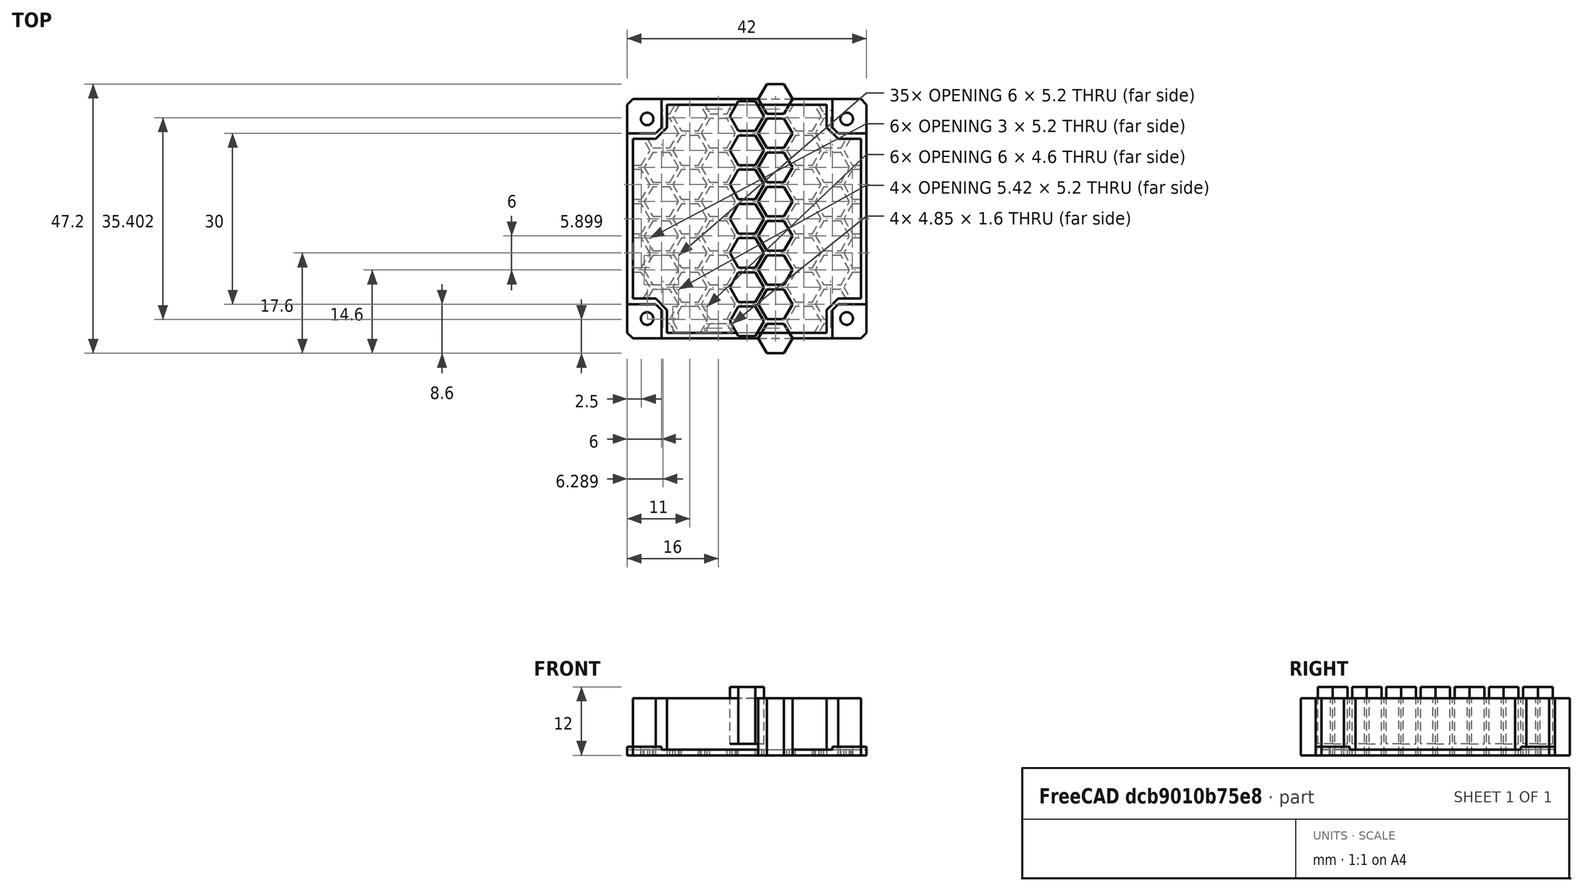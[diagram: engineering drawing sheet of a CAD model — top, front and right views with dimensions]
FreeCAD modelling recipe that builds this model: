
FCSTD DOCUMENT  (FreeCAD 0.18R14555 (Git shallow))
Label: 4010-blower-fin
License: All rights reserved
LicenseURL: http://en.wikipedia.org/wiki/All_rights_reserved
objects: Part::Feature×26, Part::Box×5, Part::Chamfer×5, Part::MultiFuse×5, Part::Cylinder×4, Part::Cut×2, Sketcher::SketchObject×1, PartDesign::Pad×1, PartDesign::Body×1, Part::MultiCommon×1
note: 52 computed .brp shape members not serialized (recipe doc carries the construction recipe); baked Part::Feature solids carry a one-line shape summary decoded from their .brp

FEATURE [Part::Box] Box  label="Cube"
  AttacherType = Attacher::AttachEngine3D
  Height = 1
  Length = 42
  Placement = pos=(-21,-21,0) rot=(0,0,1;0rad)
  Width = 42
FEATURE [Part::Box] Box001  label="Cube001"
  AttacherType = Attacher::AttachEngine3D
  Height = 1.5
  Length = 6
  Placement = pos=(-21,-21,0) rot=(0,0,1;0rad)
  Width = 6
FEATURE [Part::Box] Box002  label="Cube002"
  AttacherType = Attacher::AttachEngine3D
  Height = 1.5
  Length = 6
  Placement = pos=(-21,15,0) rot=(0,0,1;0rad)
  Width = 6
FEATURE [Part::Box] Box003  label="Cube003"
  AttacherType = Attacher::AttachEngine3D
  Height = 1.5
  Length = 6
  Placement = pos=(15,15,0) rot=(0,0,1;0rad)
  Width = 6
FEATURE [Part::Box] Box004  label="Cube004"
  AttacherType = Attacher::AttachEngine3D
  Height = 1.5
  Length = 6
  Placement = pos=(15,-21,0) rot=(0,0,1;0rad)
  Width = 6
FEATURE [Part::Cylinder] Cylinder
  Angle = 360
  AttacherType = Attacher::AttachEngine3D
  Height = 10
  Placement = pos=(-17.5,17.5,0) rot=(0,0,1;0rad)
  Radius = 1.1
FEATURE [Part::Cylinder] Cylinder001
  Angle = 360
  AttacherType = Attacher::AttachEngine3D
  Height = 10
  Placement = pos=(17.5,17.5,0) rot=(0,0,1;0rad)
  Radius = 1.1
FEATURE [Part::Cylinder] Cylinder002
  Angle = 360
  AttacherType = Attacher::AttachEngine3D
  Height = 10
  Placement = pos=(17.5,-17.5,0) rot=(0,0,1;0rad)
  Radius = 1.1
FEATURE [Part::Cylinder] Cylinder003
  Angle = 360
  AttacherType = Attacher::AttachEngine3D
  Height = 10
  Placement = pos=(-17.5,-17.5,0) rot=(0,0,1;0rad)
  Radius = 1.1
FEATURE [Part::Chamfer] Chamfer
  Base = -> Box002
  Edges = 1 edges r=1: [Edge5]
FEATURE [Part::Chamfer] Chamfer001
  Base = -> Box001
  Edges = 1 edges r=1: [Edge7]
FEATURE [Part::Chamfer] Chamfer002
  Base = -> Box003
  Edges = 1 edges r=1: [Edge1]
FEATURE [Part::Chamfer] Chamfer003
  Base = -> Box004
  Edges = 1 edges r=1: [Edge3]
FEATURE [Part::MultiFuse] Fusion
  Shapes = -> [Chamfer003,Chamfer,Chamfer001,Chamfer002,Box]
FEATURE [Part::Chamfer] Chamfer004
  Base = -> Fusion
  Edges = 4 edges r=1: [Edge19,Edge58,Edge60,Edge63]
FEATURE [Part::MultiFuse] Fusion001
  Shapes = -> [Cylinder003,Cylinder,Cylinder002,Cylinder001]
FEATURE [Part::Cut] Cut
  Base = -> Chamfer004
  Tool = -> Fusion001
FEATURE [Part::Feature] Body001  label="hex"
  shape: bbox 6 x 5.196 x 10 mm, 8 faces (baked)
FEATURE [Part::Feature] Body002  label="hex001"
  Placement = pos=(0,6,0) rot=(0,0,1;0rad)
  shape: bbox 6 x 5.196 x 10 mm, 8 faces (baked)
FEATURE [Part::Feature] Body003  label="hex002"
  Placement = pos=(0,12,0) rot=(0,0,1;0rad)
  shape: bbox 6 x 5.196 x 10 mm, 8 faces (baked)
FEATURE [Part::Feature] Body004  label="hex003"
  Placement = pos=(0,18,0) rot=(0,0,1;0rad)
  shape: bbox 6 x 5.196 x 10 mm, 8 faces (baked)
FEATURE [Part::Feature] Body005  label="hex004"
  Placement = pos=(0,-6,0) rot=(0,0,1;0rad)
  shape: bbox 6 x 5.196 x 10 mm, 8 faces (baked)
FEATURE [Part::Feature] Body006  label="hex005"
  Placement = pos=(0,-12,0) rot=(0,0,1;0rad)
  shape: bbox 6 x 5.196 x 10 mm, 8 faces (baked)
FEATURE [Part::Feature] Body007  label="hex006"
  Placement = pos=(0,-18,0) rot=(0,0,1;0rad)
  shape: bbox 6 x 5.196 x 10 mm, 8 faces (baked)
FEATURE [Part::Feature] Body008  label="hex007"
  Placement = pos=(5,3,0) rot=(0,0,1;0rad)
  shape: bbox 6 x 5.196 x 10 mm, 8 faces (baked)
FEATURE [Part::Feature] Body009  label="hex008"
  Placement = pos=(5,9,0) rot=(0,0,1;0rad)
  shape: bbox 6 x 5.196 x 10 mm, 8 faces (baked)
FEATURE [Part::Feature] Body010  label="hex009"
  Placement = pos=(5,15,0) rot=(0,0,1;0rad)
  shape: bbox 6 x 5.196 x 10 mm, 8 faces (baked)
FEATURE [Part::Feature] Body011  label="hex010"
  Placement = pos=(5,21,0) rot=(0,0,1;0rad)
  shape: bbox 6 x 5.196 x 10 mm, 8 faces (baked)
FEATURE [Part::Feature] Body012  label="hex011"
  Placement = pos=(5,-3,0) rot=(0,0,1;0rad)
  shape: bbox 6 x 5.196 x 10 mm, 8 faces (baked)
FEATURE [Part::Feature] Body013  label="hex012"
  Placement = pos=(5,-9,0) rot=(0,0,1;0rad)
  shape: bbox 6 x 5.196 x 10 mm, 8 faces (baked)
FEATURE [Part::Feature] Body014  label="hex013"
  Placement = pos=(5,-15,0) rot=(0,0,1;0rad)
  shape: bbox 6 x 5.196 x 10 mm, 8 faces (baked)
FEATURE [Part::Feature] Body015  label="hex014"
  Placement = pos=(5,-21,0) rot=(0,0,1;0rad)
  shape: bbox 6 x 5.196 x 10 mm, 8 faces (baked)
FEATURE [Part::MultiFuse] Fusion002
  Shapes = -> [Body011,Body010,Body009,Body008,Body012,Body013,Body014,Body015]
FEATURE [Part::MultiFuse] Fusion003
  Placement = pos=(0,0,2) rot=(0,0,1;0rad)
  Shapes = -> [Body004,Body003,Body002,Body001,Body005,Body006,Body007]
FEATURE [Part::Feature] Fusion002001  label="Fusion004"
  shape: bbox 6 x 47.2 x 10 mm, 64 faces, 8 solids (baked)
FEATURE [Part::Feature] Fusion003001  label="Fusion005"
  shape: bbox 6 x 41.2 x 10 mm, 56 faces, 7 solids (baked)
FEATURE [Part::Feature] Fusion003002  label="Fusion006"
  Placement = pos=(10,0,0) rot=(0,0,1;0rad)
  shape: bbox 6 x 47.2 x 10 mm, 64 faces, 8 solids (baked)
FEATURE [Part::Feature] Fusion003003  label="Fusion007"
  Placement = pos=(10,0,0) rot=(0,0,1;0rad)
  shape: bbox 6 x 41.2 x 10 mm, 56 faces, 7 solids (baked)
FEATURE [Part::Feature] Fusion003004  label="Fusion008"
  shape: bbox 6 x 47.2 x 10 mm, 64 faces, 8 solids (baked)
FEATURE [Part::Feature] Fusion003005  label="Fusion009"
  Placement = pos=(20,0,0) rot=(0,0,1;0rad)
  shape: bbox 6 x 41.2 x 10 mm, 56 faces, 7 solids (baked)
FEATURE [Part::Feature] Fusion003006  label="Fusion010"
  Placement = pos=(-10,0,0) rot=(0,0,1;0rad)
  shape: bbox 6 x 47.2 x 10 mm, 64 faces, 8 solids (baked)
FEATURE [Part::Feature] Fusion003007  label="Fusion011"
  Placement = pos=(-10,0,0) rot=(0,0,1;0rad)
  shape: bbox 6 x 41.2 x 10 mm, 56 faces, 7 solids (baked)
FEATURE [Part::Feature] Fusion003008  label="Fusion012"
  Placement = pos=(-20,0,0) rot=(0,0,1;0rad)
  shape: bbox 6 x 47.2 x 10 mm, 64 faces, 8 solids (baked)
FEATURE [Part::Feature] Fusion003009  label="Fusion013"
  Placement = pos=(-20,0,0) rot=(0,0,1;0rad)
  shape: bbox 6 x 41.2 x 10 mm, 56 faces, 7 solids (baked)
FEATURE [Part::MultiFuse] Fusion003010
  Shapes = -> [Fusion002001,Fusion003002,Fusion003008,Fusion003003,Fusion003009,Fusion003007,Fusion003006,Fusion003004,Fusion003001,Fusion003005]
FEATURE [Sketcher::SketchObject] Sketch
  MapMode = 5
  Support = -> [XY_Plane]
  sketch-geometry (16):
    g0: LineSegment StartX=-20 StartY=14 StartZ=0 EndX=-16 EndY=14 EndZ=0
    g1: LineSegment StartX=-16 StartY=14 StartZ=0 EndX=-14 EndY=16 EndZ=0
    g2: LineSegment StartX=-14 StartY=16 StartZ=0 EndX=-14 EndY=20 EndZ=0
    g3: LineSegment StartX=-14 StartY=20 StartZ=0 EndX=14 EndY=20 EndZ=0
    g4: LineSegment StartX=14 StartY=20 StartZ=0 EndX=14 EndY=16 EndZ=0
    g5: LineSegment StartX=14 StartY=16 StartZ=0 EndX=16 EndY=14 EndZ=0
    g6: LineSegment StartX=16 StartY=14 StartZ=0 EndX=20 EndY=14 EndZ=0
    g7: LineSegment StartX=20 StartY=14 StartZ=0 EndX=20 EndY=-14 EndZ=0
    g8: LineSegment StartX=20 StartY=-14 StartZ=0 EndX=16 EndY=-14 EndZ=0
    g9: LineSegment StartX=16 StartY=-14 StartZ=0 EndX=14 EndY=-16 EndZ=0
    g10: LineSegment StartX=14 StartY=-16 StartZ=0 EndX=14 EndY=-20 EndZ=0
    g11: LineSegment StartX=14 StartY=-20 StartZ=0 EndX=-14 EndY=-20 EndZ=0
    g12: LineSegment StartX=-14 StartY=-20 StartZ=0 EndX=-14 EndY=-16 EndZ=0
    g13: LineSegment StartX=-14 StartY=-16 StartZ=0 EndX=-16 EndY=-14 EndZ=0
    g14: LineSegment StartX=-16 StartY=-14 StartZ=0 EndX=-20 EndY=-14 EndZ=0
    g15: LineSegment StartX=-20 StartY=-14 StartZ=0 EndX=-20 EndY=14 EndZ=0
  constraints (28):
    c: Horizontal(g0)
    c: Coincident(g0,g1)
    c: Coincident(g1,g2)
    c: Vertical(g2)
    c: Coincident(g2,g3)
    c: Horizontal(g3)
    c: Coincident(g3,g4)
    c: Vertical(g4)
    c: Coincident(g4,g5)
    c: Coincident(g5,g6)
    c: Horizontal(g6)
    c: Coincident(g6,g7)
    c: Vertical(g7)
    c: Coincident(g7,g8)
    c: Horizontal(g8)
    c: Coincident(g8,g9)
    c: Coincident(g9,g10)
    c: Vertical(g10)
    c: Coincident(g10,g11)
    c: Horizontal(g11)
    c: Coincident(g11,g12)
    c: Vertical(g12)
    c: Coincident(g12,g13)
    c: Coincident(g13,g14)
    c: Horizontal(g14)
    c: Coincident(g14,g15)
    c: Coincident(g15,g0)
    c: Vertical(g15)
FEATURE [PartDesign::Pad] Pad
  Length = 10
  Length2 = 100
  Profile = -> Sketch
  Type = 0
FEATURE [PartDesign::Body] Body
  Group = -> [Sketch,Pad]
  Origin = -> Origin
  Tip = -> Pad
FEATURE [Part::Feature] Body016  label="Body001"
  shape: bbox 40 x 40 x 10 mm, 18 faces (baked)
FEATURE [Part::MultiCommon] Common
  Shapes = -> [Fusion003010,Body016]
FEATURE [Part::Cut] Cut001
  Base = -> Cut
  Tool = -> Common
